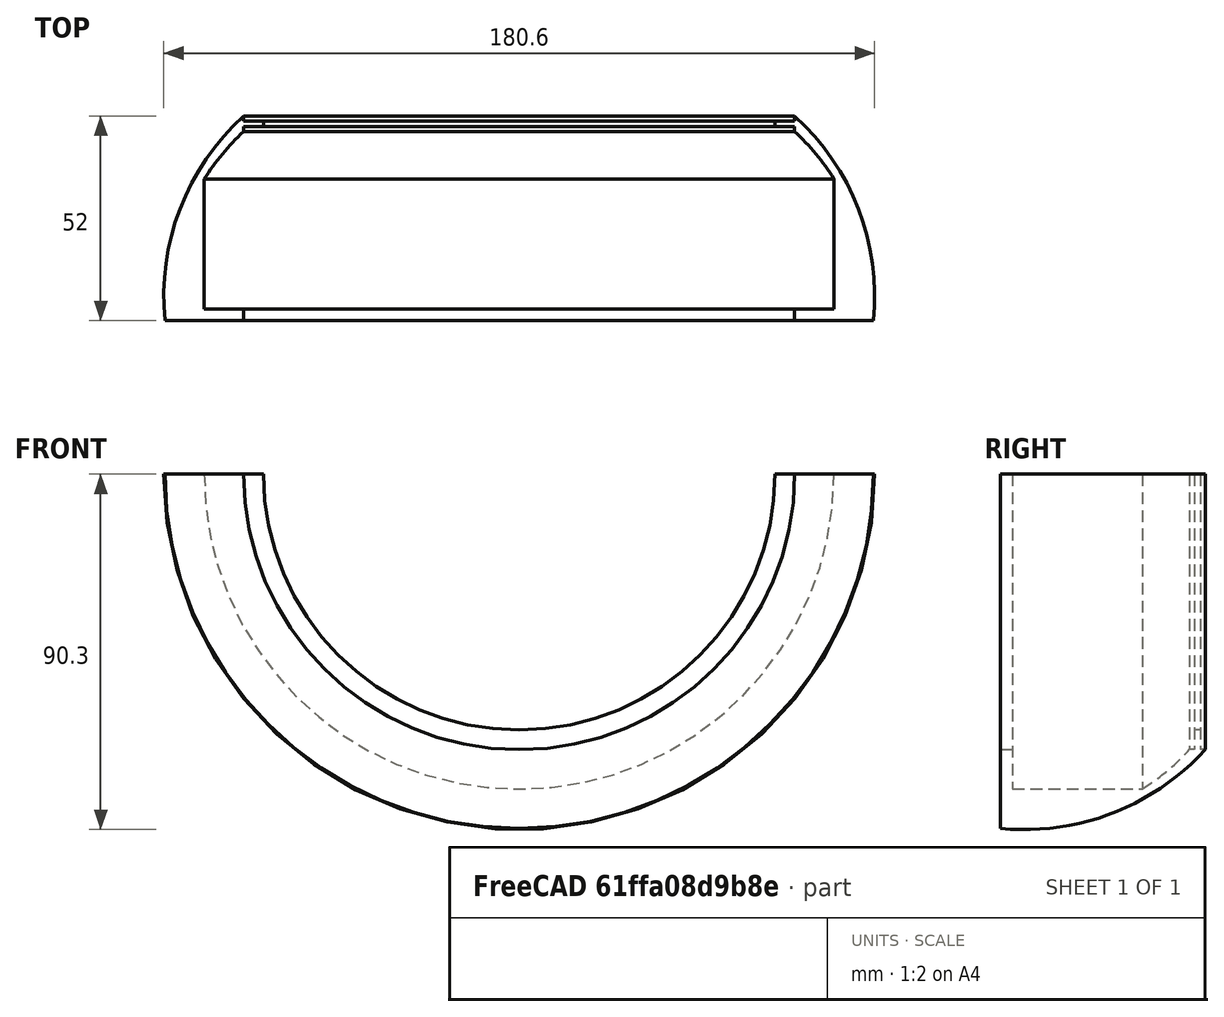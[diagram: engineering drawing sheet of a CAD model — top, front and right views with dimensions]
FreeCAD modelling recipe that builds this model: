
FCSTD DOCUMENT
Label: base2
objects: Part::Feature×2, Sketcher::SketchObject×1, Part::Revolution×1
note: 4 computed .brp shape members not serialized (recipe doc carries the construction recipe); baked Part::Feature solids carry a one-line shape summary decoded from their .brp

FEATURE [Sketcher::SketchObject] Sketch
  sketch-geometry (11):
    g0: LineSegment StartX=70 StartY=0 StartZ=0 EndX=90 EndY=0 EndZ=0
    g1: LineSegment StartX=70 StartY=0 StartZ=0 EndX=70 EndY=3 EndZ=0
    g2: LineSegment StartX=70 StartY=3 StartZ=0 EndX=80 EndY=3 EndZ=0
    g3: LineSegment StartX=70 StartY=52 StartZ=0 EndX=70 EndY=50.75 EndZ=0
    g4: LineSegment StartX=70 StartY=50.75 StartZ=0 EndX=65 EndY=50.75 EndZ=0
    g5: LineSegment StartX=65 StartY=50.75 StartZ=0 EndX=65 EndY=49.25 EndZ=0
    g6: LineSegment StartX=65 StartY=49.25 StartZ=0 EndX=70 EndY=49.25 EndZ=0
    g7: LineSegment StartX=80 StartY=3 StartZ=0 EndX=80 EndY=36 EndZ=0
    g8: ArcOfCircle CenterX=30.0738 CenterY=4.56153 CenterZ=0 NormalX=0 NormalY=0 NormalZ=1 Radius=59 StartAngle=0.561971 EndAngle=0.827505
    g9: LineSegment StartX=70 StartY=49.25 StartZ=0 EndX=70 EndY=48 EndZ=0
    g10: ArcOfCircle CenterX=28.3024 CenterY=6.11632 CenterZ=0 NormalX=0 NormalY=0 NormalZ=1 Radius=62 StartAngle=6.18437 EndAngle=7.11634
  constraints (35):
    c: Horizontal(g0)
    c: PointOnObject(g0,g-1)
    c: Distance(g0) = 20
    c: Distance(g-1,g0) = 70
    c: Coincident(g1,g0)
    c: Vertical(g1)
    c: Coincident(g2,g1)
    c: Horizontal(g2)
    c: Vertical(g3)
    c: Distance(g1) = 3
    c: Distance(g2) = 10
    c: Distance(g0,g3) = 52
    c: Distance(g3) = 1.25
    c: Coincident(g4,g3)
    c: Horizontal(g4)
    c: Coincident(g5,g4)
    c: Vertical(g5)
    c: Coincident(g6,g5)
    c: Horizontal(g6)
    c: Distance(g5) = 1.5
    c: Distance(g6) = 5
    c: Distance(g4) = 5
    c: DistanceX(g3,g0) = 0
    c: Coincident(g7,g2)
    c: Vertical(g7)
    c: Distance(g7) = 33
    c: Coincident(g8,g7)
    c: Radius(g8) = 59
    c: Vertical(g9)
    c: Coincident(g9,g6)
    c: Distance(g9) = 1.25
    c: Coincident(g8,g9)
    c: Coincident(g10,g0)
    c: Radius(g10) = 62
    c: Coincident(g10,g3)
FEATURE [Part::Revolution] Revolve
  Angle = 180
  Axis = (0,1,0)
  Base = (0,0,0)
  Source = -> Sketch
FEATURE [Part::Feature] Face
  shape: bbox 25.3 x 52 x 2e-07 mm, 1 faces, 0 solids (baked)
FEATURE [Part::Feature] Face001
  shape: bbox 25.3 x 52 x 2e-07 mm, 1 faces, 0 solids (baked)
